# Revit family: FireFighting_Fire-Hydrant-Landing-Valve_Galvin_STORZ-NSW_RG
name_source: partatom
category: Pipe Accessories
revit_build: Autodesk Revit MEP 2012 (Build: 20110916_2132(x64)
units: mm (PartAtom-declared; Revit-internal decimal feet)

## types (1)
- 381255RGRE
    Assembly Code = D2090800
    Description = Red Emperor Fire Hydrant Landing Valve Storz [NSW] - Roll Groove Inlet with Cap
    DimHeight = 200 mm  [stored 0.656168 ft]
    FilterObject_ANZRS = 381255
    FlowRate = 0.00 L/s
    Inlet = 80mm Roll Groove Inlet
    Instructions = http://www.galvinengineering.com.au
    Keynote = 15400
    Manufacturer = Galvin Engineering
    Model = 381255RGRE
    ModifiedIssue_ANZRS = 20140330 $
    Outlet = 64mm QLD Fire Brigade Thread
    StyleOrType_ANZRS = Pipe Accessory - Valve
    Type Comments = 381255RGRE
    URL = www.galvinengineering.com.au

note: [stored X ft] marks values corroborated as IEEE doubles in the binary element streams (Revit-internal decimal feet)

## geometry (parser evidence)
native form markers: Blend x6, Sweep x1
no freeform markers — native parametric forms only
